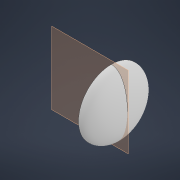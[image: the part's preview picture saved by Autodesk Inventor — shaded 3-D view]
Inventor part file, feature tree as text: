
AUTODESK INVENTOR PART (.ipt)
format: ipt  version: 2022 (Build 260153000, 153)  size: 444,416 bytes
history: native  units: in
note: dims shown in document units (in); Inventor stores cm internally (conversion verified against a paired STEP export)
features: sketch x2, revolve x1, extrude x1, other x1
ambient origin geometry x8: Origin, YZ Plane, XZ Plane, XY Plane, X Axis, Y Axis, Z Axis, Center Point
bodies: Solid1 (feature_tree)
feature tree (5):
  revolve  "Revolution1"  Angle=90.0deg
  extrude  "Extrusion1"  [1 undecoded]
  sketch  "Sketch1"  dims[d0=0.0in d1=0.7874in d2=90.0deg]
  other  "2D Equation Curve1"
  sketch  "Sketch2"  dims[d3=5.0in d4=0.0in]
note: 1 required parameter value undecoded (feature->parameter linkage not recoverable at this tier; creation-order binding heuristic only, values carry confidence <= 0.55)
